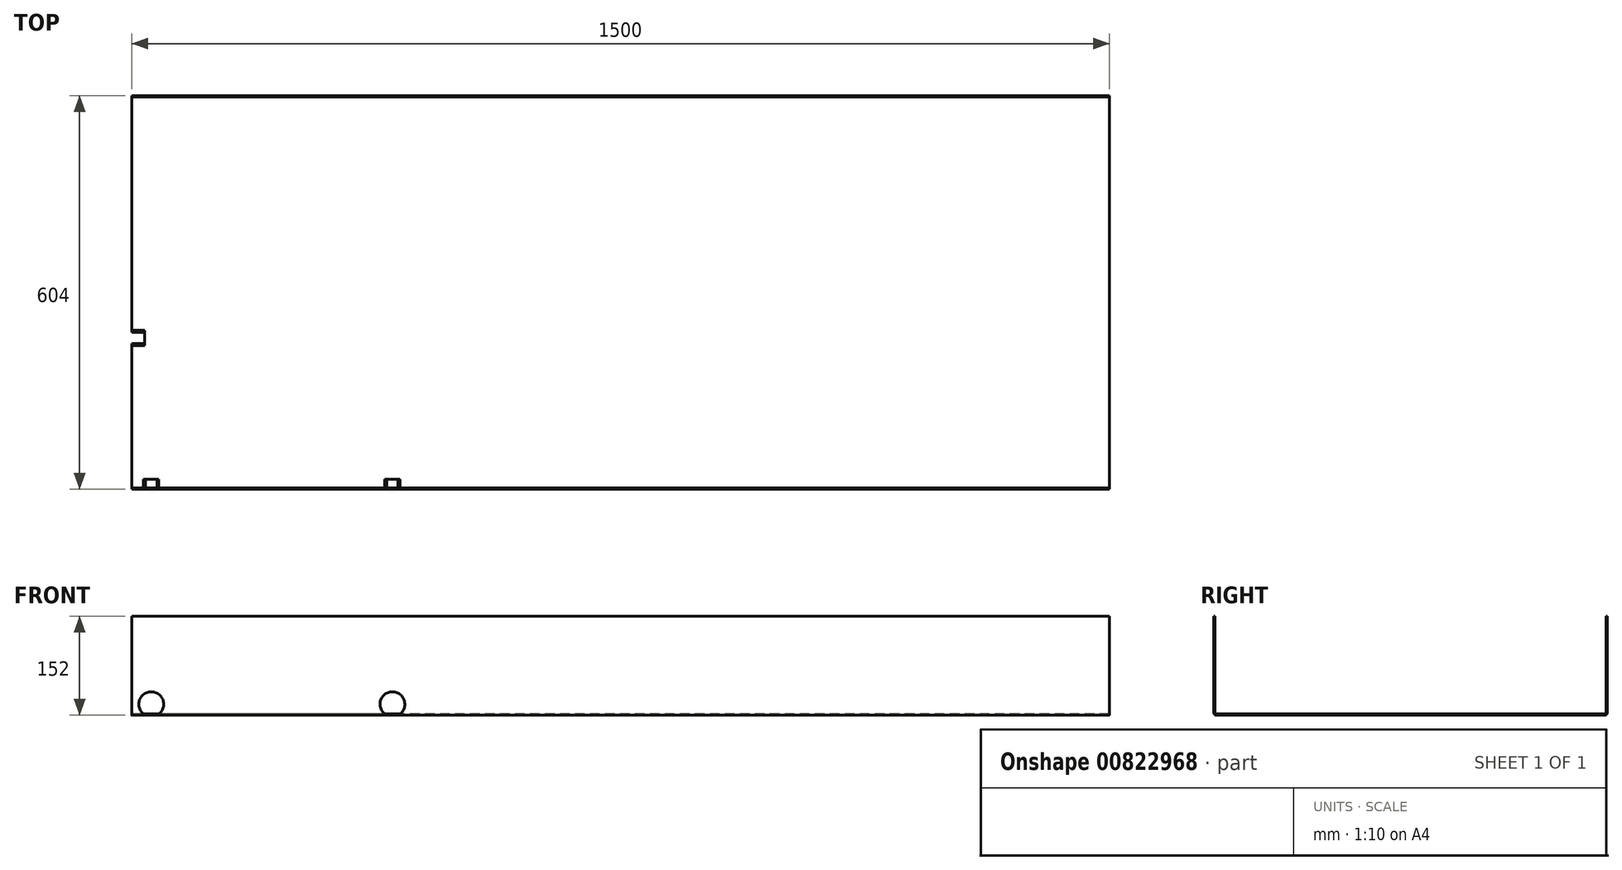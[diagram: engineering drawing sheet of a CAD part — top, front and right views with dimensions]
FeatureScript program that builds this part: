
annotation { "Feature Type Name" : "Feature", "Feature Type Description" : "" }
export const myFeature = defineFeature(function(context is Context, id is Id, definition is map)
    precondition{}
    {
        {
            var Q0;
            Q0=qCreatedBy(makeId("Right.planeOp"),FACE);
            var sketch = newSketch(context, id + "F0", { "sketchPlane" : qUnion([Q0])});
            skLineSegment(sketch, "E0.bottom", {"start": v(-300, -75) * mm, "end": v(300, -75) * mm});
            skLineSegment(sketch, "E0.top", {"start": v(-300, 75) * mm, "end": v(300, 75) * mm, "construction": true});
            skLineSegment(sketch, "E0.left", {"start": v(-300, -75) * mm, "end": v(-300, 75) * mm});
            skLineSegment(sketch, "E0.right", {"start": v(300, -75) * mm, "end": v(300, 75) * mm});
            skPoint(sketch, "E0.middle", {"position": v(0, 0) * mm});
            skLineSegment(sketch, "E1.0", {"start": v(-302, -77) * mm, "end": v(-302, 75) * mm});
            skLineSegment(sketch, "E1.1", {"start": v(-302, -77) * mm, "end": v(302, -77) * mm});
            skLineSegment(sketch, "E1.2", {"start": v(302, -77) * mm, "end": v(302, 75) * mm});
            skLineSegment(sketch, "E2", {"start": v(-302, 75) * mm, "end": v(-300, 75) * mm});
            skLineSegment(sketch, "E3", {"start": v(302, 75) * mm, "end": v(300, 75) * mm});
            skSolve(sketch);
        }
        {
            var Q0;
            Q0 = qSketchRegion(id + "F0", true);
            extrude(context, id + "F1", {"entities" : qUnion([Q0]), "endBound" : BoundingType.SYMMETRIC, "depth" : 1500 * mm, "offsetDistance" : 25 * mm});
        }
        {
            var Q0;
            Q0=makeQuery(id+"F1.opExtrude","SWEPT_EDGE",EDGE,{"disambiguationData":[OSD([sQuery(id+"F0.wireOp",EDGE,"E0.bottom"),sQuery(id+"F0.wireOp",EDGE,"E0.right")])]});
            var Q1;
            Q1=makeQuery(id+"F1.opExtrude","SWEPT_EDGE",EDGE,{"disambiguationData":[OSD([sQuery(id+"F0.wireOp",EDGE,"E0.bottom"),sQuery(id+"F0.wireOp",EDGE,"E0.left")])]});
            fillet(context, id + "F2", {"entities" : qUnion([Q0, Q1]), "radius" : 2 * mm, "tangentPropagation" : true, "allowEdgeOverflow" : false});
        }
        {
            var Q0;
            Q0=makeQuery(id+"F1.opExtrude","SWEPT_EDGE",EDGE,{"disambiguationData":[OSD([sQuery(id+"F0.wireOp",EDGE,"E1.0"),sQuery(id+"F0.wireOp",EDGE,"E1.1")])]});
            var Q1;
            Q1=makeQuery(id+"F1.opExtrude","SWEPT_EDGE",EDGE,{"disambiguationData":[OSD([sQuery(id+"F0.wireOp",EDGE,"E1.1"),sQuery(id+"F0.wireOp",EDGE,"E1.2")])]});
            fillet(context, id + "F3", {"entities" : qUnion([Q0, Q1]), "radius" : 4 * mm, "tangentPropagation" : true, "allowEdgeOverflow" : false});
        }
        {
            var Q0;
            Q0=makeQuery(id+"F1.opExtrude","SWEPT_FACE",FACE,{"disambiguationData":[OSD([sQuery(id+"F0.wireOp",EDGE,"E1.0")])]});
            var sketch = newSketch(context, id + "F4", { "sketchPlane" : qUnion([Q0])});
            skLineSegment(sketch, "E4.0", {"start": v(-750, -73) * mm, "end": v(-750, 75) * mm, "construction": true});
            skLineSegment(sketch, "E5.0", {"start": v(750, -77) * mm, "end": v(-750, -77) * mm, "construction": true});
            skLineSegment(sketch, "E6.0", {"start": v(750, 75) * mm, "end": v(-750, 75) * mm, "construction": true});
            skCircle(sketch, "E7", {"center": v(-720, -60) * mm, "radius": 19.05 * mm});
            skLineSegment(sketch, "E8", {"start": v(-720, -60) * mm, "end": v(-350, -60) * mm, "construction": true});
            skCircle(sketch, "E9", {"center": v(-350, -60) * mm, "radius": 19.05 * mm});
            skCircle(sketch, "E10", {"center": v(-720, -60) * mm, "radius": 15.35 * mm, "construction": true});
            skSolve(sketch);
        }
        {
            var Q0;
            Q0 = qSketchRegion(id + "F4", true);
            extrude(context, id + "F5", {"entities" : qUnion([Q0]), "operationType" : NewBodyOperationType.REMOVE, "oppositeDirection" : true, "depth" : 15 * mm, "offsetDistance" : 25 * mm});
        }
        {
            var Q0;
            Q0=makeQuery(id+"F1.opExtrude","CAP_FACE",FACE,{"disambiguationData":[OSD([sQuery(id+"F0.wireOp",EDGE,"E0.bottom"),sQuery(id+"F0.wireOp",EDGE,"E0.left"),sQuery(id+"F0.wireOp",EDGE,"E0.right"),sQuery(id+"F0.wireOp",EDGE,"E1.0"),sQuery(id+"F0.wireOp",EDGE,"E1.1"),sQuery(id+"F0.wireOp",EDGE,"E1.2"),sQuery(id+"F0.wireOp",EDGE,"E2"),sQuery(id+"F0.wireOp",EDGE,"E3")])],"isStart":true});
            var sketch = newSketch(context, id + "F6", { "sketchPlane" : qUnion([Q0])});
            skLineSegment(sketch, "E11.0", {"start": v(300, -73) * mm, "end": v(300, 75) * mm, "construction": true});
            skLineSegment(sketch, "E12.0", {"start": v(298, -77) * mm, "end": v(-298, -77) * mm, "construction": true});
            skCircle(sketch, "E13", {"center": v(70, -60) * mm, "radius": 19.05 * mm});
            skSolve(sketch);
        }
        {
            var Q0;
            Q0 = qSketchRegion(id + "F6", true);
            extrude(context, id + "F7", {"entities" : qUnion([Q0]), "operationType" : NewBodyOperationType.REMOVE, "oppositeDirection" : true, "depth" : 20 * mm, "offsetDistance" : 25 * mm});
        }
    });
